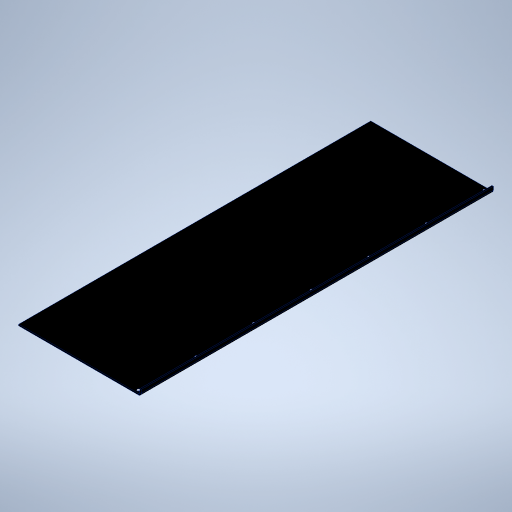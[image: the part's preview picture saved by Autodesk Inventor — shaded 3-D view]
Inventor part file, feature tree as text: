
AUTODESK INVENTOR PART (.ipt)
format: ipt  version: 2023 (Build 270158000, 158)  size: 265,728 bytes
history: native  units: in
note: dims shown in document units (in); Inventor stores cm internally (conversion verified against a paired STEP export)
features: sheet_metal_op x4, sketch x3, other x2, hole x1, pattern_linear x1
ambient origin geometry x8: Origin, YZ Plane, XZ Plane, XY Plane, X Axis, Y Axis, Z Axis, Center Point
bodies: Solid1 (feature_tree)
feature tree (11):
  sheet_metal_op  "Face1"
  sheet_metal_op  "Flange1"
  hole  "Hole1"  [1 undecoded]
  pattern_linear  "Rectangular Pattern1"  Spacing1=0.0875in  [1 undecoded]
  sketch  "Sketch1"  dims[d0=7.6378in d1=22.4409in]
  other  "Plate1"
  sketch  "Sketch3"  dims[d2=3.8189in]
  other  "Plate2"
  sheet_metal_op  "Bend1"
  sheet_metal_op  "Corner1"
  sketch  "Sketch4"  dims[d3=11.2205in d4=0.0875in d5=0.0875in d6=0.0438in d7=0.175in d8=0.0875in d9=0.3937in d10=90.0deg d11=0.0875in d12=0.35in d13=0.0875in d14=0.0875in d15=0.194in d16=0.2953in d17=0.1476in d18=0.0984in d19=90.0deg d20=0.0875in d21=0.8108in d22=0.1939in d23=2.7559in d25=3.6755in]
note: 2 required parameter values undecoded (feature->parameter linkage not recoverable at this tier; creation-order binding heuristic only, values carry confidence <= 0.55)
